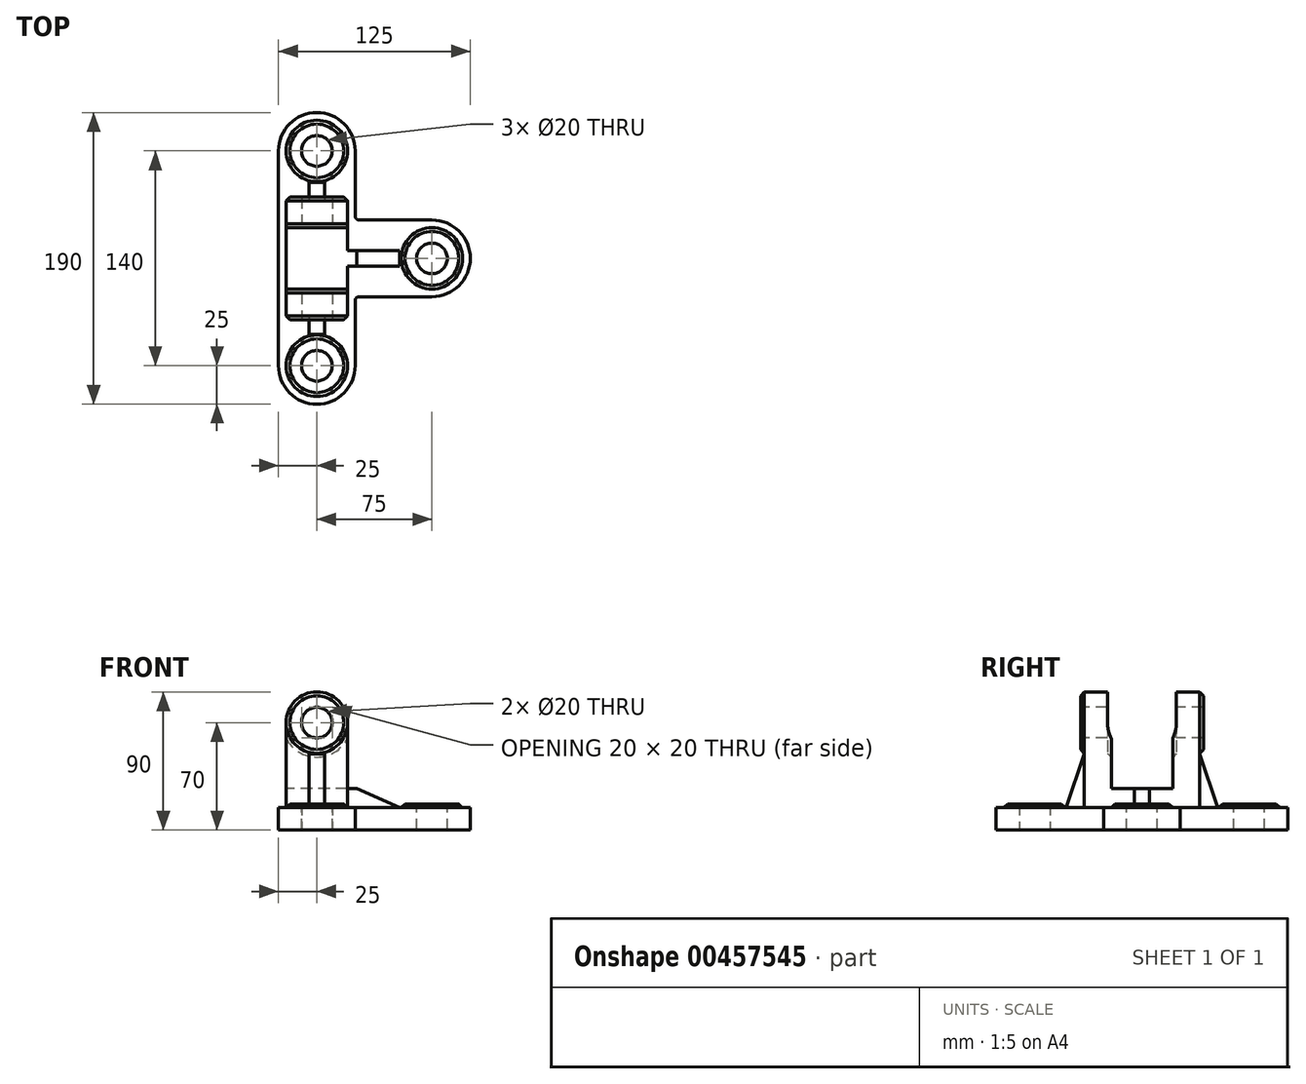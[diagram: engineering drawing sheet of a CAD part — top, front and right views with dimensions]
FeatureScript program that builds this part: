
annotation { "Feature Type Name" : "Feature", "Feature Type Description" : "" }
export const myFeature = defineFeature(function(context is Context, id is Id, definition is map)
    precondition{}
    {
        {
            var Q0;
            Q0=qCreatedBy(makeId("Top.planeOp"),FACE);
            var sketch = newSketch(context, id + "F0", { "sketchPlane" : qUnion([Q0])});
            skLineSegment(sketch, "E0", {"start": v(-25, 70) * mm, "end": v(-25, -70) * mm});
            skLineSegment(sketch, "E1", {"start": v(25, -70) * mm, "end": v(25, -25) * mm});
            skLineSegment(sketch, "E2", {"start": v(25, -25) * mm, "end": v(75, -25) * mm});
            skLineSegment(sketch, "E3", {"start": v(25, 70) * mm, "end": v(25, 25) * mm});
            skLineSegment(sketch, "E4", {"start": v(25, 25) * mm, "end": v(75, 25) * mm});
            skArc(sketch, "E5", {"start": v(75, 25) * mm, "mid": v(100, 0) * mm, "end": v(75, -25) * mm});
            skArc(sketch, "E6", {"start": v(-25, 70) * mm, "mid": v(0, 95) * mm, "end": v(25, 70) * mm});
            skArc(sketch, "E7", {"start": v(-25, -70) * mm, "mid": v(0, -95) * mm, "end": v(25, -70) * mm});
            skSolve(sketch);
        }
        {
            var Q0;
            Q0=makeQuery(id+"F0.imprint","IMPRINT",FACE,{"disambiguationData":[TD([[makeQuery(id+"F0.imprint","IMPRINT",EDGE,{"derivedFrom":sQuery(id+"F0.wireOp",EDGE,"E0")}),1.0]])]});
            extrude(context, id + "F1", {"entities" : qUnion([Q0]), "depth" : 14.5 * mm});
        }
        {
            var Q0;
            Q0=qCreatedBy(makeId("Right.planeOp"),FACE);
            var sketch = newSketch(context, id + "F2", { "sketchPlane" : qUnion([Q0])});
            skLineSegment(sketch, "E8", {"start": v(-37.5, 0) * mm, "end": v(-37.5, 70) * mm});
            skLineSegment(sketch, "E9", {"start": v(-37.5, 70) * mm, "end": v(-22.5, 70) * mm});
            skLineSegment(sketch, "E10", {"start": v(-22.5, 70) * mm, "end": v(-22.5, 27) * mm});
            skLineSegment(sketch, "E11", {"start": v(-22.5, 27) * mm, "end": v(22.5, 27) * mm});
            skLineSegment(sketch, "E12", {"start": v(22.5, 27) * mm, "end": v(22.5, 70) * mm});
            skLineSegment(sketch, "E13", {"start": v(22.5, 70) * mm, "end": v(37.5, 70) * mm});
            skLineSegment(sketch, "E14", {"start": v(37.5, 70) * mm, "end": v(37.5, 0) * mm});
            skLineSegment(sketch, "E15", {"start": v(37.5, 0) * mm, "end": v(-37.5, 0) * mm});
            skSolve(sketch);
        }
        {
            var Q0;
            Q0=makeQuery(id+"F2.imprint","IMPRINT",FACE,{"disambiguationData":[TD([[makeQuery(id+"F2.imprint","IMPRINT",EDGE,{"derivedFrom":sQuery(id+"F2.wireOp",EDGE,"E8")}),-1.0]])]});
            extrude(context, id + "F3", {"entities" : qUnion([Q0]), "operationType" : NewBodyOperationType.ADD, "endBound" : BoundingType.SYMMETRIC, "depth" : 40 * mm});
        }
        {
            var Q0;
            Q0=qCreatedBy(makeId("Right.planeOp"),FACE);
            var sketch = newSketch(context, id + "F4", { "sketchPlane" : qUnion([Q0])});
            skLineSegment(sketch, "E16", {"start": v(-49.5, 14.5) * mm, "end": v(-37.5, 14.5) * mm});
            skLineSegment(sketch, "E17", {"start": v(-37.5, 14.5) * mm, "end": v(-37.5, 49.5) * mm});
            skLineSegment(sketch, "E18", {"start": v(-37.5, 49.5) * mm, "end": v(-49.5, 14.5) * mm});
            skLineSegment(sketch, "E19", {"start": v(37.5, 14.5) * mm, "end": v(49.5, 14.5) * mm});
            skLineSegment(sketch, "E20", {"start": v(49.5, 14.5) * mm, "end": v(37.5, 49.5) * mm});
            skLineSegment(sketch, "E21", {"start": v(37.5, 49.5) * mm, "end": v(37.5, 14.5) * mm});
            skSolve(sketch);
        }
        {
            var Q0;
            Q0=makeQuery(id+"F4.imprint","IMPRINT",FACE,{"disambiguationData":[TD([[makeQuery(id+"F4.imprint","IMPRINT",EDGE,{"derivedFrom":sQuery(id+"F4.wireOp",EDGE,"E16")}),1.0]])]});
            var Q1;
            Q1=makeQuery(id+"F4.imprint","IMPRINT",FACE,{"disambiguationData":[TD([[makeQuery(id+"F4.imprint","IMPRINT",EDGE,{"derivedFrom":sQuery(id+"F4.wireOp",EDGE,"E19")}),1.0]])]});
            extrude(context, id + "F5", {"entities" : qUnion([Q0, Q1]), "operationType" : NewBodyOperationType.ADD, "endBound" : BoundingType.SYMMETRIC, "depth" : 10 * mm});
        }
        {
            var Q0;
            Q0=qCreatedBy(makeId("Front.planeOp"),FACE);
            var sketch = newSketch(context, id + "F6", { "sketchPlane" : qUnion([Q0])});
            skLineSegment(sketch, "E22", {"start": v(20, 27) * mm, "end": v(20, 14.5) * mm});
            skLineSegment(sketch, "E23", {"start": v(20, 14.5) * mm, "end": v(54, 14.5) * mm});
            skLineSegment(sketch, "E24", {"start": v(54, 14.5) * mm, "end": v(26, 27) * mm});
            skLineSegment(sketch, "E25", {"start": v(26, 27) * mm, "end": v(20, 27) * mm});
            skSolve(sketch);
        }
        {
            var Q0;
            Q0=makeQuery(id+"F6.imprint","IMPRINT",FACE,{"disambiguationData":[TD([[makeQuery(id+"F6.imprint","IMPRINT",EDGE,{"derivedFrom":sQuery(id+"F6.wireOp",EDGE,"E22")}),1.0]])]});
            extrude(context, id + "F7", {"entities" : qUnion([Q0]), "operationType" : NewBodyOperationType.ADD, "endBound" : BoundingType.SYMMETRIC, "depth" : 10 * mm});
        }
        {
            var Q0;
            Q0=makeQuery(id+"F3.opExtrude","SWEPT_FACE",FACE,{"disambiguationData":[OSD([sQuery(id+"F2.wireOp",EDGE,"E8")])]});
            var sketch = newSketch(context, id + "F8", { "sketchPlane" : qUnion([Q0])});
            skCircle(sketch, "E26", {"center": v(0, 70) * mm, "radius": 20 * mm});
            skSolve(sketch);
        }
        {
            var Q0;
            {var subQ1=sQuery(id+"F2.wireOp",EDGE,"E8");var subQ2=makeQuery(id+"F3.opExtrude","SWEPT_EDGE",EDGE,{"disambiguationData":[OSD([subQ1,sQuery(id+"F2.wireOp",EDGE,"E9")])]});Q0=makeQuery(id+"F8.imprint","IMPRINT",FACE,{"disambiguationData":[TD([[makeQuery(id+"F8.imprint","IMPRINT",EDGE,{"derivedFrom":subQ2}),1.0]])]});}
            var Q1;
            {var subQ1=sQuery(id+"F2.wireOp",EDGE,"E8");var subQ2=makeQuery(id+"F3.opExtrude","SWEPT_EDGE",EDGE,{"disambiguationData":[OSD([subQ1,sQuery(id+"F2.wireOp",EDGE,"E9")])]});Q1=makeQuery(id+"F8.imprint","IMPRINT",FACE,{"disambiguationData":[TD([[makeQuery(id+"F8.imprint","IMPRINT",EDGE,{"derivedFrom":subQ2}),-1.0]])]});}
            extrude(context, id + "F9", {"entities" : qUnion([Q0, Q1]), "operationType" : NewBodyOperationType.ADD, "depth" : 2.5 * mm});
        }
        {
            var Q0;
            Q0=makeQuery(id+"F9.opExtrude","CAP_FACE",FACE,{"disambiguationData":[OSD([sQuery(id+"F8.wireOp",EDGE,"E26")])],"isStart":true});
            extrude(context, id + "F10", {"entities" : qUnion([Q0]), "operationType" : NewBodyOperationType.ADD, "depth" : 15 * mm});
        }
        {
            var Q0;
            Q0=makeQuery(id+"F10.boolean.opBoolean","MERGE",FACE,{"derivedFrom":[makeQuery(id+"F3.opExtrude","SWEPT_FACE",FACE,{"disambiguationData":[OSD([sQuery(id+"F2.wireOp",EDGE,"E10")])]}),makeQuery(id+"F10.opExtrude","CAP_FACE",FACE,{"disambiguationData":[OSD([sQuery(id+"F8.wireOp",EDGE,"E26")])],"isStart":false})]});
            var sketch = newSketch(context, id + "F11", { "sketchPlane" : qUnion([Q0])});
            skCircle(sketch, "E27", {"center": v(0, 70) * mm, "radius": 20 * mm});
            skSolve(sketch);
        }
        {
            var Q0;
            {var subQ0=sQuery(id+"F11.wireOp",EDGE,"E27");Q0=makeQuery(id+"F11.imprint","IMPRINT",FACE,{"disambiguationData":[TD([[makeQuery(id+"F11.imprint","IMPRINT",EDGE,{"disambiguationData":[OD(0.0)],"derivedFrom":subQ0}),-1.0]])]});}
            extrude(context, id + "F12", {"entities" : qUnion([Q0]), "operationType" : NewBodyOperationType.ADD, "depth" : 2.5 * mm});
        }
        {
            var Q0;
            Q0=makeQuery(id+"F12.opExtrude","CAP_EDGE",EDGE,{"disambiguationData":[OSD([sQuery(id+"F11.wireOp",EDGE,"E27")])],"isStart":false});
            chamfer(context, id + "F13", {"entities" : qUnion([Q0]), "width" : 2.5 * mm, "tangentPropagation" : true});
        }
        {
            var Q0;
            Q0=makeQuery(id+"F9.opExtrude","CAP_EDGE",EDGE,{"disambiguationData":[OSD([sQuery(id+"F8.wireOp",EDGE,"E26")])],"isStart":false});
            chamfer(context, id + "F14", {"entities" : qUnion([Q0]), "width" : 2.5 * mm, "tangentPropagation" : true});
        }
        {
            var Q0;
            Q0=makeQuery(id+"F3.opExtrude","SWEPT_FACE",FACE,{"disambiguationData":[OSD([sQuery(id+"F2.wireOp",EDGE,"E14")])]});
            var sketch = newSketch(context, id + "F15", { "sketchPlane" : qUnion([Q0])});
            skCircle(sketch, "E28", {"center": v(0, 70) * mm, "radius": 20 * mm});
            skSolve(sketch);
        }
        {
            var Q0;
            {var subQ1=sQuery(id+"F2.wireOp",EDGE,"E14");var subQ2=makeQuery(id+"F3.opExtrude","SWEPT_EDGE",EDGE,{"disambiguationData":[OSD([sQuery(id+"F2.wireOp",EDGE,"E13"),subQ1])]});Q0=makeQuery(id+"F15.imprint","IMPRINT",FACE,{"disambiguationData":[TD([[makeQuery(id+"F15.imprint","IMPRINT",EDGE,{"derivedFrom":subQ2}),1.0]])]});}
            var Q1;
            {var subQ1=sQuery(id+"F2.wireOp",EDGE,"E14");var subQ2=makeQuery(id+"F3.opExtrude","SWEPT_EDGE",EDGE,{"disambiguationData":[OSD([sQuery(id+"F2.wireOp",EDGE,"E13"),subQ1])]});Q1=makeQuery(id+"F15.imprint","IMPRINT",FACE,{"disambiguationData":[TD([[makeQuery(id+"F15.imprint","IMPRINT",EDGE,{"derivedFrom":subQ2}),-1.0]])]});}
            extrude(context, id + "F16", {"entities" : qUnion([Q0, Q1]), "operationType" : NewBodyOperationType.ADD, "oppositeDirection" : true, "depth" : 15 * mm});
        }
        {
            var Q0;
            Q0=makeQuery(id+"F16.boolean.opBoolean","MERGE",FACE,{"derivedFrom":[makeQuery(id+"F3.opExtrude","SWEPT_FACE",FACE,{"disambiguationData":[OSD([sQuery(id+"F2.wireOp",EDGE,"E14")])]}),makeQuery(id+"F16.opExtrude","CAP_FACE",FACE,{"disambiguationData":[OSD([sQuery(id+"F15.wireOp",EDGE,"E28")])],"isStart":true})]});
            var sketch = newSketch(context, id + "F17", { "sketchPlane" : qUnion([Q0])});
            skCircle(sketch, "E29", {"center": v(0, 70) * mm, "radius": 20 * mm});
            skSolve(sketch);
        }
        {
            var Q0;
            {var subQ0=sQuery(id+"F17.wireOp",EDGE,"E29");var subQ1=sQuery(id+"F2.wireOp",EDGE,"E14");var subQ2=makeQuery(id+"F17.imprint","INTERSECT",VERTEX,{"derivedFrom":[makeQuery(id+"F3.opExtrude","CAP_EDGE",EDGE,{"disambiguationData":[OSD([subQ1])],"isStart":true}),subQ0]});Q0=makeQuery(id+"F17.imprint","IMPRINT",FACE,{"disambiguationData":[TD([[makeQuery(id+"F17.imprint","IMPRINT",EDGE,{"disambiguationData":[TD([[subQ2,-1.0]])],"derivedFrom":subQ0}),1.0]])]});}
            extrude(context, id + "F18", {"entities" : qUnion([Q0]), "operationType" : NewBodyOperationType.ADD, "depth" : 2.5 * mm});
        }
        {
            var Q0;
            Q0=makeQuery(id+"F16.boolean.opBoolean","MERGE",FACE,{"derivedFrom":[makeQuery(id+"F3.opExtrude","SWEPT_FACE",FACE,{"disambiguationData":[OSD([sQuery(id+"F2.wireOp",EDGE,"E12")])]}),makeQuery(id+"F16.opExtrude","CAP_FACE",FACE,{"disambiguationData":[OSD([sQuery(id+"F15.wireOp",EDGE,"E28")])],"isStart":false})]});
            var sketch = newSketch(context, id + "F19", { "sketchPlane" : qUnion([Q0])});
            skCircle(sketch, "E30", {"center": v(0, 70) * mm, "radius": 20 * mm});
            skSolve(sketch);
        }
        {
            var Q0;
            {var subQ0=sQuery(id+"F19.wireOp",EDGE,"E30");Q0=makeQuery(id+"F19.imprint","IMPRINT",FACE,{"disambiguationData":[TD([[makeQuery(id+"F19.imprint","IMPRINT",EDGE,{"disambiguationData":[OD(0.0)],"derivedFrom":subQ0}),-1.0]])]});}
            var Q1;
            Q1=makeQuery(id+"F18.opExtrude","CAP_FACE",FACE,{"disambiguationData":[OSD([sQuery(id+"F17.wireOp",EDGE,"E29")])],"isStart":false});
            extrude(context, id + "F20", {"entities" : qUnion([Q0, Q1]), "operationType" : NewBodyOperationType.ADD, "depth" : 2.5 * mm});
        }
        {
            var Q0;
            Q0=makeQuery(id+"F18.opExtrude","CAP_EDGE",EDGE,{"disambiguationData":[OSD([sQuery(id+"F17.wireOp",EDGE,"E29")])],"isStart":false});
            var Q1;
            Q1=makeQuery(id+"F20.opExtrude","CAP_EDGE",EDGE,{"disambiguationData":[OSD([sQuery(id+"F19.wireOp",EDGE,"E30")])],"isStart":false});
            chamfer(context, id + "F21", {"entities" : qUnion([Q0, Q1]), "width" : 2.5 * mm, "tangentPropagation" : true});
        }
        {
            var Q0;
            Q0=makeQuery(id+"F1.opExtrude","CAP_FACE",FACE,{"disambiguationData":[OSD([sQuery(id+"F0.wireOp",EDGE,"E0"),sQuery(id+"F0.wireOp",EDGE,"E1"),sQuery(id+"F0.wireOp",EDGE,"E2"),sQuery(id+"F0.wireOp",EDGE,"E3"),sQuery(id+"F0.wireOp",EDGE,"E4"),sQuery(id+"F0.wireOp",EDGE,"E5"),sQuery(id+"F0.wireOp",EDGE,"E6"),sQuery(id+"F0.wireOp",EDGE,"E7")])],"isStart":false});
            var sketch = newSketch(context, id + "F22", { "sketchPlane" : qUnion([Q0])});
            skCircle(sketch, "E31", {"center": v(0, 70) * mm, "radius": 20 * mm});
            skCircle(sketch, "E32", {"center": v(75, 0) * mm, "radius": 20 * mm});
            skCircle(sketch, "E33", {"center": v(0, -70) * mm, "radius": 20 * mm});
            skSolve(sketch);
        }
        {
            var Q0;
            Q0=makeQuery(id+"F22.imprint","IMPRINT",FACE,{"disambiguationData":[TD([[makeQuery(id+"F22.imprint","IMPRINT",EDGE,{"derivedFrom":sQuery(id+"F22.wireOp",EDGE,"E31")}),1.0]])]});
            var Q1;
            Q1=makeQuery(id+"F22.imprint","IMPRINT",FACE,{"disambiguationData":[TD([[makeQuery(id+"F22.imprint","IMPRINT",EDGE,{"derivedFrom":sQuery(id+"F22.wireOp",EDGE,"E32")}),1.0]])]});
            var Q2;
            Q2=makeQuery(id+"F22.imprint","IMPRINT",FACE,{"disambiguationData":[TD([[makeQuery(id+"F22.imprint","IMPRINT",EDGE,{"derivedFrom":sQuery(id+"F22.wireOp",EDGE,"E33")}),1.0]])]});
            extrude(context, id + "F23", {"entities" : qUnion([Q0, Q1, Q2]), "operationType" : NewBodyOperationType.ADD, "depth" : 2.5 * mm});
        }
        {
            var Q0;
            Q0=makeQuery(id+"F23.opExtrude","CAP_EDGE",EDGE,{"disambiguationData":[OSD([sQuery(id+"F22.wireOp",EDGE,"E31")])],"isStart":false});
            var Q1;
            Q1=makeQuery(id+"F23.opExtrude","CAP_EDGE",EDGE,{"disambiguationData":[OSD([sQuery(id+"F22.wireOp",EDGE,"E32")])],"isStart":false});
            var Q2;
            Q2=makeQuery(id+"F23.opExtrude","CAP_EDGE",EDGE,{"disambiguationData":[OSD([sQuery(id+"F22.wireOp",EDGE,"E33")])],"isStart":false});
            chamfer(context, id + "F24", {"entities" : qUnion([Q0, Q1, Q2]), "width" : 2.5 * mm, "tangentPropagation" : true});
        }
        {
            var Q0;
            Q0=makeQuery(id+"F23.opExtrude","CAP_FACE",FACE,{"disambiguationData":[OSD([sQuery(id+"F22.wireOp",EDGE,"E31")])],"isStart":false});
            var sketch = newSketch(context, id + "F25", { "sketchPlane" : qUnion([Q0])});
            skCircle(sketch, "E34", {"center": v(0, 70) * mm, "radius": 10 * mm});
            skSolve(sketch);
        }
        {
            var Q0;
            Q0=makeQuery(id+"F25.imprint","IMPRINT",FACE,{"disambiguationData":[TD([[makeQuery(id+"F25.imprint","IMPRINT",EDGE,{"derivedFrom":sQuery(id+"F25.wireOp",EDGE,"E34")}),1.0]])]});
            extrude(context, id + "F26", {"entities" : qUnion([Q0]), "operationType" : NewBodyOperationType.REMOVE, "endBound" : BoundingType.THROUGH_ALL, "oppositeDirection" : true, "depth" : 25 * mm});
        }
        {
            var Q0;
            Q0=makeQuery(id+"F23.opExtrude","CAP_FACE",FACE,{"disambiguationData":[OSD([sQuery(id+"F22.wireOp",EDGE,"E32")])],"isStart":false});
            var sketch = newSketch(context, id + "F27", { "sketchPlane" : qUnion([Q0])});
            skCircle(sketch, "E35", {"center": v(75, 0) * mm, "radius": 10 * mm});
            skSolve(sketch);
        }
        {
            var Q0;
            Q0=makeQuery(id+"F27.imprint","IMPRINT",FACE,{"disambiguationData":[TD([[makeQuery(id+"F27.imprint","IMPRINT",EDGE,{"derivedFrom":sQuery(id+"F27.wireOp",EDGE,"E35")}),1.0]])]});
            extrude(context, id + "F28", {"entities" : qUnion([Q0]), "operationType" : NewBodyOperationType.REMOVE, "endBound" : BoundingType.THROUGH_ALL, "oppositeDirection" : true, "depth" : 25 * mm});
        }
        {
            var Q0;
            Q0=makeQuery(id+"F9.opExtrude","CAP_FACE",FACE,{"disambiguationData":[OSD([sQuery(id+"F8.wireOp",EDGE,"E26")])],"isStart":false});
            var sketch = newSketch(context, id + "F29", { "sketchPlane" : qUnion([Q0])});
            skCircle(sketch, "E36", {"center": v(0, 70) * mm, "radius": 10 * mm});
            skSolve(sketch);
        }
        {
            var Q0;
            Q0=makeQuery(id+"F29.imprint","IMPRINT",FACE,{"disambiguationData":[TD([[makeQuery(id+"F29.imprint","IMPRINT",EDGE,{"derivedFrom":sQuery(id+"F29.wireOp",EDGE,"E36")}),1.0]])]});
            extrude(context, id + "F30", {"entities" : qUnion([Q0]), "operationType" : NewBodyOperationType.REMOVE, "endBound" : BoundingType.THROUGH_ALL, "oppositeDirection" : true, "depth" : 25 * mm});
        }
        {
            var Q0;
            Q0=makeQuery(id+"F1.opExtrude","CAP_FACE",FACE,{"disambiguationData":[OSD([sQuery(id+"F0.wireOp",EDGE,"E0"),sQuery(id+"F0.wireOp",EDGE,"E1"),sQuery(id+"F0.wireOp",EDGE,"E2"),sQuery(id+"F0.wireOp",EDGE,"E3"),sQuery(id+"F0.wireOp",EDGE,"E4"),sQuery(id+"F0.wireOp",EDGE,"E5"),sQuery(id+"F0.wireOp",EDGE,"E6"),sQuery(id+"F0.wireOp",EDGE,"E7")])],"isStart":false});
            var sketch = newSketch(context, id + "F31", { "sketchPlane" : qUnion([Q0])});
            skCircle(sketch, "E37", {"center": v(0, -70) * mm, "radius": 10 * mm});
            skSolve(sketch);
        }
        {
            var Q0;
            Q0 = qSketchRegion(id + "F31", true);
            extrude(context, id + "F32", {"entities" : qUnion([Q0]), "operationType" : NewBodyOperationType.REMOVE, "endBound" : BoundingType.THROUGH_ALL, "depth" : 25 * mm});
        }
        {
            var Q0;
            Q0=makeQuery(id+"F1.opExtrude","CAP_FACE",FACE,{"disambiguationData":[OSD([sQuery(id+"F0.wireOp",EDGE,"E0"),sQuery(id+"F0.wireOp",EDGE,"E1"),sQuery(id+"F0.wireOp",EDGE,"E2"),sQuery(id+"F0.wireOp",EDGE,"E3"),sQuery(id+"F0.wireOp",EDGE,"E4"),sQuery(id+"F0.wireOp",EDGE,"E5"),sQuery(id+"F0.wireOp",EDGE,"E6"),sQuery(id+"F0.wireOp",EDGE,"E7")])],"isStart":true});
            var sketch = newSketch(context, id + "F33", { "sketchPlane" : qUnion([Q0])});
            skCircle(sketch, "E38", {"center": v(0, 70) * mm, "radius": 10 * mm});
            skSolve(sketch);
        }
        {
            var Q0;
            Q0=makeQuery(id+"F33.imprint","IMPRINT",FACE,{"disambiguationData":[TD([[makeQuery(id+"F33.imprint","IMPRINT",EDGE,{"derivedFrom":sQuery(id+"F33.wireOp",EDGE,"E38")}),1.0]])]});
            extrude(context, id + "F34", {"entities" : qUnion([Q0]), "operationType" : NewBodyOperationType.REMOVE, "endBound" : BoundingType.THROUGH_ALL, "oppositeDirection" : true, "depth" : 25 * mm});
        }
        {
            var Q0;
            Q0=makeQuery(id+"F3.opExtrude","SWEPT_EDGE",EDGE,{"disambiguationData":[OSD([sQuery(id+"F2.wireOp",EDGE,"E11"),sQuery(id+"F2.wireOp",EDGE,"E12")])]});
            var Q1;
            Q1=makeQuery(id+"F3.opExtrude","SWEPT_EDGE",EDGE,{"disambiguationData":[OSD([sQuery(id+"F2.wireOp",EDGE,"E10"),sQuery(id+"F2.wireOp",EDGE,"E11")])]});
            var Q2;
            Q2=makeQuery(id+"F1.opExtrude","SWEPT_EDGE",EDGE,{"disambiguationData":[OSD([sQuery(id+"F0.wireOp",EDGE,"E3"),sQuery(id+"F0.wireOp",EDGE,"E4")])]});
            var Q3;
            Q3=makeQuery(id+"F1.opExtrude","SWEPT_EDGE",EDGE,{"disambiguationData":[OSD([sQuery(id+"F0.wireOp",EDGE,"E1"),sQuery(id+"F0.wireOp",EDGE,"E2")])]});
            fillet(context, id + "F35", {"entities" : qUnion([Q0, Q1, Q2, Q3]), "radius" : 2.5 * mm, "tangentPropagation" : true, "allowEdgeOverflow" : false});
        }
    });
